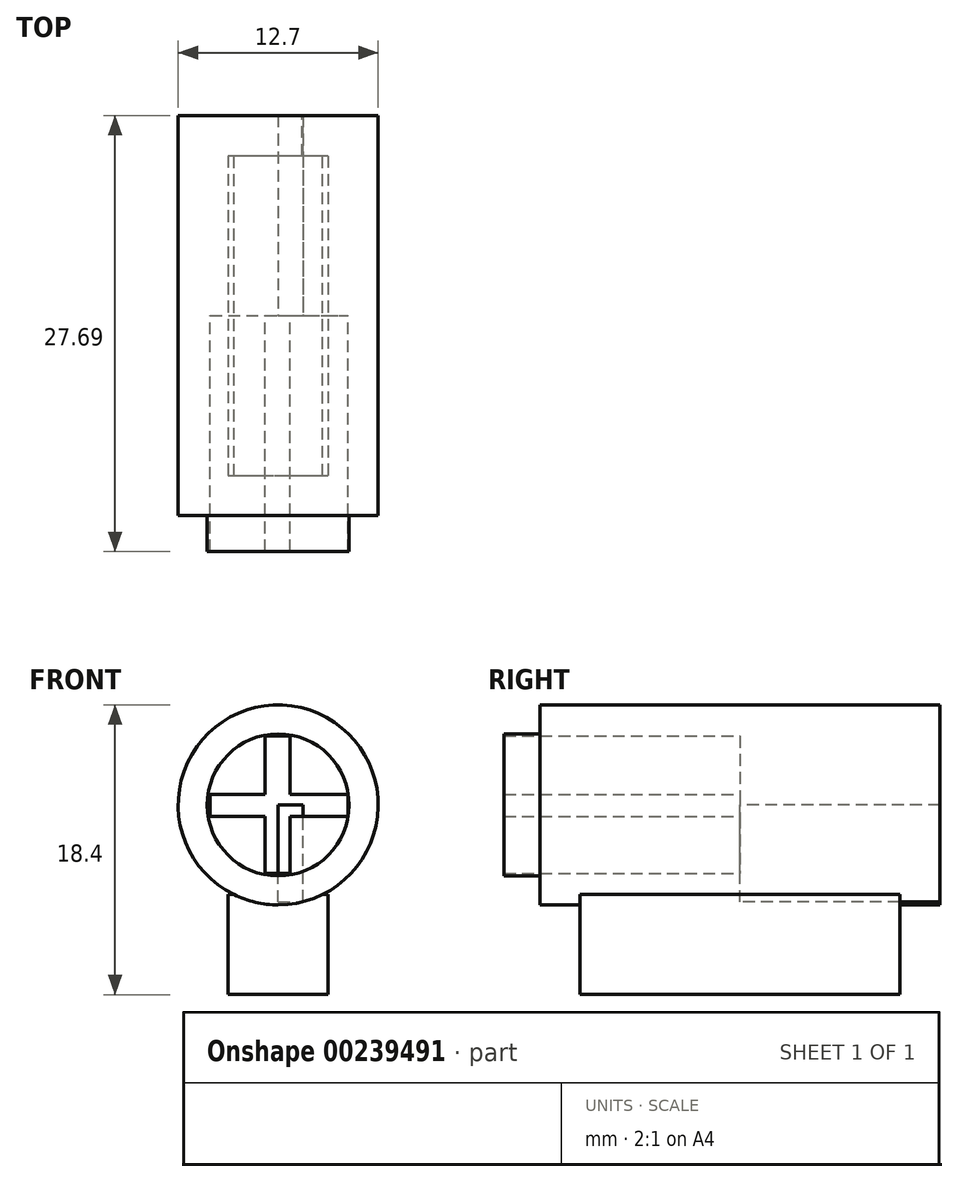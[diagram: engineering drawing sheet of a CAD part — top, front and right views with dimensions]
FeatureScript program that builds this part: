
annotation { "Feature Type Name" : "Feature", "Feature Type Description" : "" }
export const myFeature = defineFeature(function(context is Context, id is Id, definition is map)
    precondition{}
    {
        {
            var Q0;
            Q0=qCreatedBy(makeId("Front.planeOp"),FACE);
            var sketch = newSketch(context, id + "F0", { "sketchPlane" : qUnion([Q0])});
            skCircle(sketch, "E0", {"center": v(0, 0) * mm, "radius": 6.35 * mm});
            skSolve(sketch);
        }
        {
            var Q0;
            Q0 = qSketchRegion(id + "F0", true);
            extrude(context, id + "F1", {"entities" : qUnion([Q0]), "endBound" : BoundingType.SYMMETRIC, "depth" : 25.4 * mm});
        }
        {
            var Q0;
            Q0=qCreatedBy(makeId("Right.planeOp"),FACE);
            var sketch = newSketch(context, id + "F2", { "sketchPlane" : qUnion([Q0])});
            skLineSegment(sketch, "E1.bottom", {"start": v(10.14, -5.7) * mm, "end": v(-10.18, -5.7) * mm});
            skLineSegment(sketch, "E1.top", {"start": v(10.14, -12.05) * mm, "end": v(-10.18, -12.05) * mm});
            skLineSegment(sketch, "E1.left", {"start": v(10.14, -5.7) * mm, "end": v(10.14, -12.05) * mm});
            skLineSegment(sketch, "E1.right", {"start": v(-10.18, -5.7) * mm, "end": v(-10.18, -12.05) * mm});
            skSolve(sketch);
        }
        {
            var Q0;
            Q0 = qSketchRegion(id + "F2", true);
            extrude(context, id + "F3", {"entities" : qUnion([Q0]), "operationType" : NewBodyOperationType.ADD, "endBound" : BoundingType.SYMMETRIC, "depth" : 6.35 * mm});
        }
        {
            var Q0;
            Q0=qCreatedBy(makeId("Front.planeOp"),FACE);
            var sketch = newSketch(context, id + "F4", { "sketchPlane" : qUnion([Q0])});
            skLineSegment(sketch, "E2.bottom", {"start": v(0, -6.17) * mm, "end": v(1.57, -6.17) * mm});
            skLineSegment(sketch, "E2.top", {"start": v(0, 0) * mm, "end": v(1.57, 0) * mm});
            skLineSegment(sketch, "E2.left", {"start": v(0, -6.17) * mm, "end": v(0, 0) * mm});
            skLineSegment(sketch, "E2.right", {"start": v(1.57, -6.17) * mm, "end": v(1.57, 0) * mm});
            skSolve(sketch);
        }
        {
            var Q0;
            Q0 = qSketchRegion(id + "F4", true);
            extrude(context, id + "F5", {"entities" : qUnion([Q0]), "operationType" : NewBodyOperationType.REMOVE, "oppositeDirection" : true, "depth" : 40.13 * mm});
        }
        {
            var Q0;
            Q0=qCreatedBy(makeId("Front.planeOp"),FACE);
            var sketch = newSketch(context, id + "F6", { "sketchPlane" : qUnion([Q0])});
            skCircle(sketch, "E3", {"center": v(0, 0) * mm, "radius": 4.5 * mm});
            skSolve(sketch);
        }
        {
            var Q0;
            Q0 = qSketchRegion(id + "F6", true);
            extrude(context, id + "F7", {"entities" : qUnion([Q0]), "operationType" : NewBodyOperationType.ADD, "depth" : 15 * mm});
        }
        {
            var Q0;
            Q0=qCreatedBy(makeId("Front.planeOp"),FACE);
            var sketch = newSketch(context, id + "F8", { "sketchPlane" : qUnion([Q0])});
            skLineSegment(sketch, "E4.bottom", {"start": v(-4.31, 0.66) * mm, "end": v(4.43, 0.66) * mm});
            skLineSegment(sketch, "E4.top", {"start": v(-4.31, -0.73) * mm, "end": v(4.43, -0.73) * mm});
            skLineSegment(sketch, "E4.left", {"start": v(-4.31, 0.66) * mm, "end": v(-4.31, -0.73) * mm});
            skLineSegment(sketch, "E4.right", {"start": v(4.43, 0.66) * mm, "end": v(4.43, -0.73) * mm});
            skSolve(sketch);
        }
        {
            var Q0;
            Q0 = qSketchRegion(id + "F8", true);
            extrude(context, id + "F9", {"entities" : qUnion([Q0]), "operationType" : NewBodyOperationType.REMOVE, "depth" : 22.86 * mm});
        }
        {
            var Q0;
            Q0=qCreatedBy(makeId("Front.planeOp"),FACE);
            var sketch = newSketch(context, id + "F10", { "sketchPlane" : qUnion([Q0])});
            skLineSegment(sketch, "E5.bottom", {"start": v(-0.83, 4.39) * mm, "end": v(0.74, 4.39) * mm});
            skLineSegment(sketch, "E5.top", {"start": v(-0.83, -4.35) * mm, "end": v(0.74, -4.35) * mm});
            skLineSegment(sketch, "E5.left", {"start": v(-0.83, 4.39) * mm, "end": v(-0.83, -4.35) * mm});
            skLineSegment(sketch, "E5.right", {"start": v(0.74, 4.39) * mm, "end": v(0.74, -4.35) * mm});
            skSolve(sketch);
        }
        {
            var Q0;
            Q0 = qSketchRegion(id + "F10", true);
            extrude(context, id + "F11", {"entities" : qUnion([Q0]), "operationType" : NewBodyOperationType.REMOVE, "depth" : 37.08 * mm});
        }
    });
